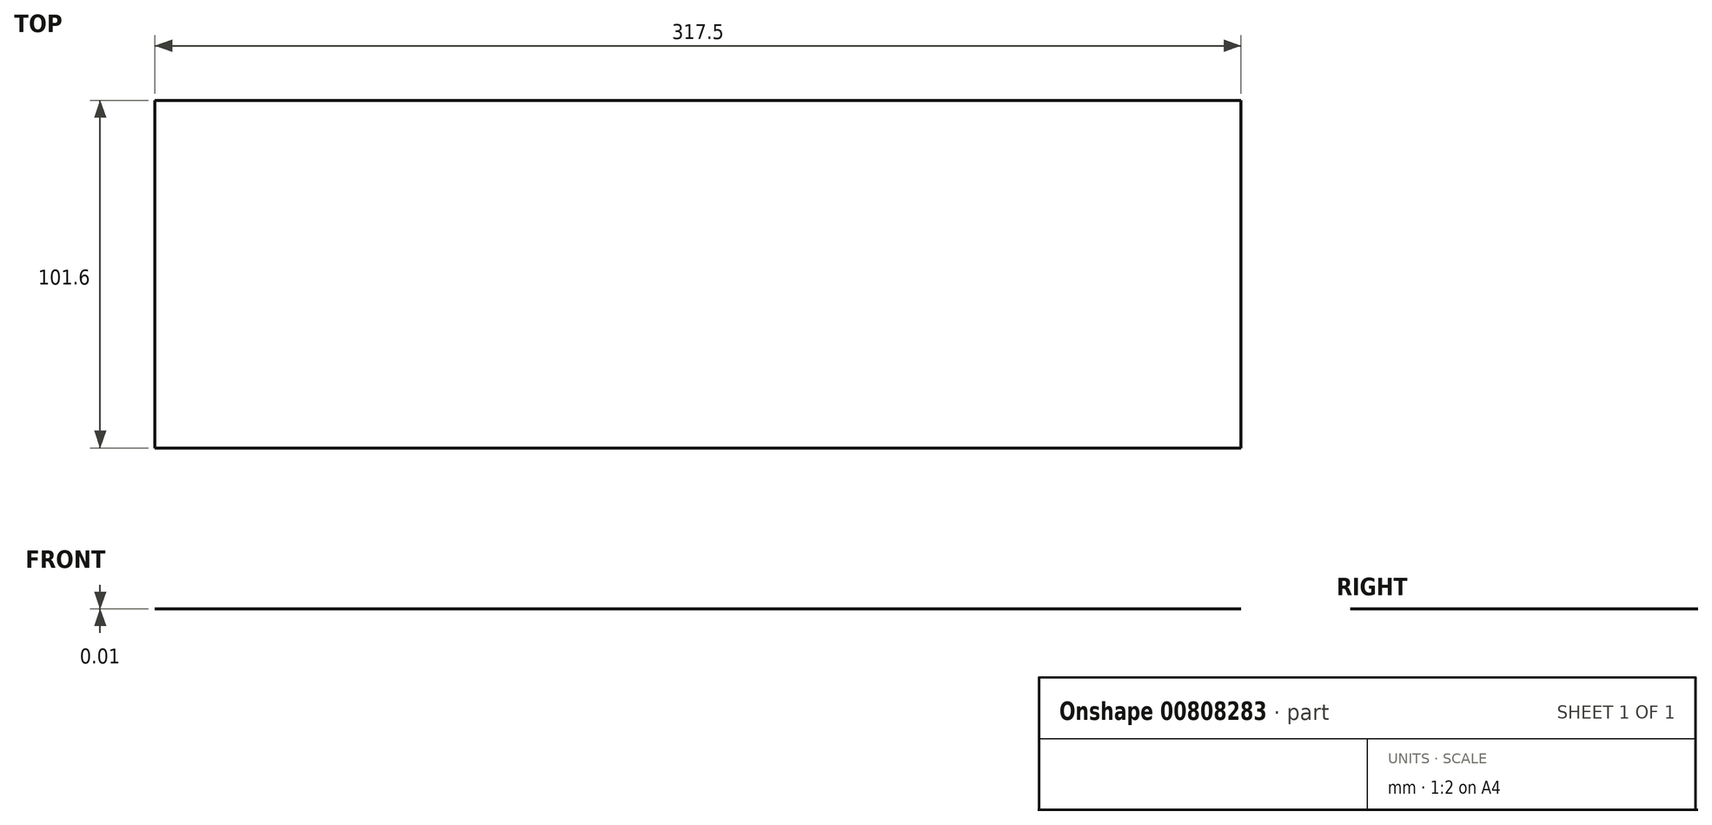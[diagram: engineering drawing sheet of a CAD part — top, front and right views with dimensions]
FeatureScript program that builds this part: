
annotation { "Feature Type Name" : "Feature", "Feature Type Description" : "" }
export const myFeature = defineFeature(function(context is Context, id is Id, definition is map)
    precondition{}
    {
        {
            var Q0;
            Q0=qCreatedBy(makeId("Top.planeOp"),FACE);
            var sketch = newSketch(context, id + "F0", { "sketchPlane" : qUnion([Q0])});
            skLineSegment(sketch, "E0.bottom", {"start": v(158.75, -50.8) * mm, "end": v(-158.75, -50.8) * mm});
            skLineSegment(sketch, "E0.top", {"start": v(158.75, 50.8) * mm, "end": v(-158.75, 50.8) * mm});
            skLineSegment(sketch, "E0.left", {"start": v(158.75, -50.8) * mm, "end": v(158.75, 50.8) * mm});
            skLineSegment(sketch, "E0.right", {"start": v(-158.75, -50.8) * mm, "end": v(-158.75, 50.8) * mm});
            skPoint(sketch, "E0.middle", {"position": v(0, 0) * mm});
            skSolve(sketch);
        }
        {
            var Q0;
            Q0 = qSketchRegion(id + "F0", true);
            extrude(context, id + "F1", {"entities" : qUnion([Q0]), "depth" : 3 / 203.2 * mm, "offsetDistance" : 25 * mm});
        }
    });
